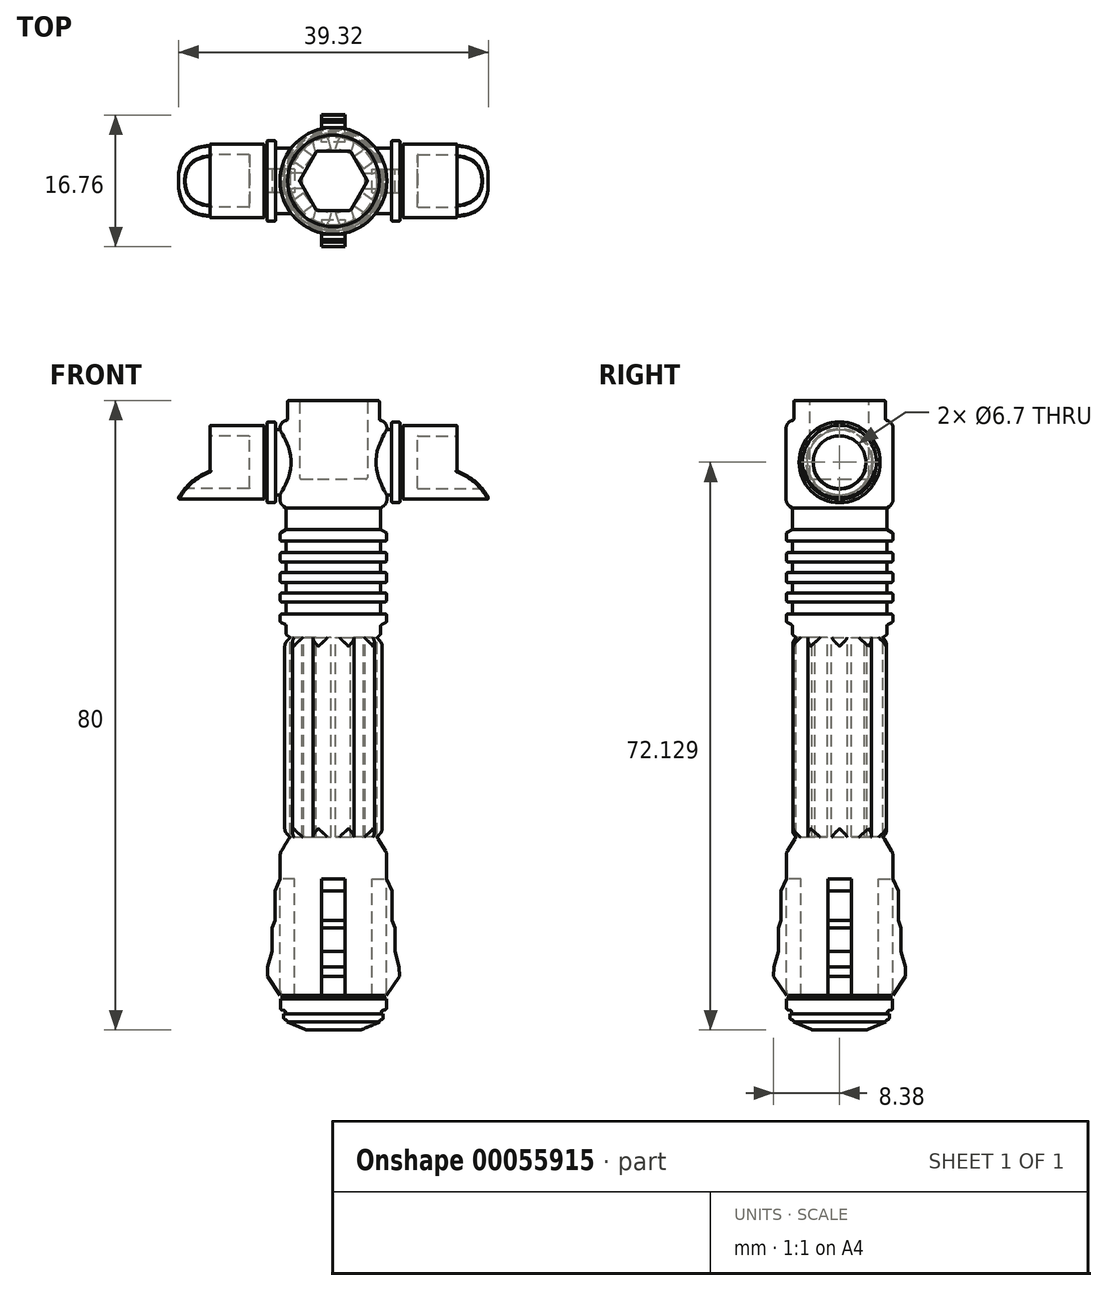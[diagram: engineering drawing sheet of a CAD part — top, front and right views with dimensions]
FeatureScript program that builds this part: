
annotation { "Feature Type Name" : "Feature", "Feature Type Description" : "" }
export const myFeature = defineFeature(function(context is Context, id is Id, definition is map)
    precondition{}
    {
        {
            var Q0;
            Q0=qCreatedBy(makeId("Front.planeOp"),FACE);
            var sketch = newSketch(context, id + "F0", { "sketchPlane" : qUnion([Q0])});
            skLineSegment(sketch, "E0", {"start": v(0, 45.09) * mm, "end": v(5.82, 45.09) * mm});
            skLineSegment(sketch, "E1", {"start": v(5.82, 45.09) * mm, "end": v(5.82, 42.56) * mm});
            skLineSegment(sketch, "E2", {"start": v(5.82, 42.56) * mm, "end": v(6.78, 42.56) * mm});
            skLineSegment(sketch, "E3", {"start": v(6.78, 42.56) * mm, "end": v(6.78, 31.92) * mm});
            skLineSegment(sketch, "E4", {"start": v(6.78, 31.92) * mm, "end": v(6, 31.43) * mm});
            skLineSegment(sketch, "E5", {"start": v(6, 31.43) * mm, "end": v(6, 28.66) * mm});
            skLineSegment(sketch, "E6", {"start": v(6, 28.66) * mm, "end": v(6.75, 28.26) * mm});
            skLineSegment(sketch, "E7", {"start": v(6.75, 28.26) * mm, "end": v(6.75, 27.2) * mm});
            skLineSegment(sketch, "E8", {"start": v(6.75, 27.2) * mm, "end": v(6, 27.2) * mm});
            skLineSegment(sketch, "E9", {"start": v(6, 27.2) * mm, "end": v(6, 25.75) * mm});
            skLineSegment(sketch, "E10", {"start": v(6, 25.75) * mm, "end": v(6.75, 25.75) * mm});
            skLineSegment(sketch, "E11", {"start": v(6.75, 25.75) * mm, "end": v(6.75, 24.56) * mm});
            skLineSegment(sketch, "E12", {"start": v(6.75, 24.56) * mm, "end": v(6, 24.56) * mm});
            skLineSegment(sketch, "E13", {"start": v(6, 24.56) * mm, "end": v(6, 23.2) * mm});
            skLineSegment(sketch, "E14", {"start": v(6, 23.2) * mm, "end": v(6.75, 23.2) * mm});
            skLineSegment(sketch, "E15", {"start": v(6.75, 23.2) * mm, "end": v(6.75, 21.94) * mm});
            skLineSegment(sketch, "E16", {"start": v(6.75, 21.94) * mm, "end": v(6, 21.94) * mm});
            skLineSegment(sketch, "E17", {"start": v(6, 21.94) * mm, "end": v(6, 20.62) * mm});
            skLineSegment(sketch, "E18", {"start": v(6, 20.62) * mm, "end": v(6.75, 20.62) * mm});
            skLineSegment(sketch, "E19", {"start": v(6.75, 20.62) * mm, "end": v(6.75, 19.49) * mm});
            skLineSegment(sketch, "E20", {"start": v(6.75, 19.49) * mm, "end": v(6, 19.49) * mm});
            skLineSegment(sketch, "E21", {"start": v(6, 19.49) * mm, "end": v(6, 17.96) * mm});
            skLineSegment(sketch, "E22", {"start": v(6, 17.96) * mm, "end": v(6.75, 17.96) * mm});
            skLineSegment(sketch, "E23", {"start": v(6.75, 17.96) * mm, "end": v(6.75, 16.93) * mm});
            skLineSegment(sketch, "E24", {"start": v(6.75, 16.93) * mm, "end": v(6, 16.54) * mm});
            skLineSegment(sketch, "E25", {"start": v(5.52, -10.4) * mm, "end": v(6.75, -12.38) * mm});
            skLineSegment(sketch, "E26", {"start": v(6.75, -12.38) * mm, "end": v(6.75, -30.53) * mm});
            skLineSegment(sketch, "E27", {"start": v(6.75, -30.53) * mm, "end": v(6.5, -30.53) * mm});
            skLineSegment(sketch, "E28", {"start": v(6.5, -30.53) * mm, "end": v(6.5, -30.96) * mm});
            skLineSegment(sketch, "E29", {"start": v(6.5, -30.96) * mm, "end": v(6.72, -30.96) * mm});
            skLineSegment(sketch, "E30", {"start": v(6.72, -30.96) * mm, "end": v(6.72, -32.3) * mm});
            skLineSegment(sketch, "E31", {"start": v(6.72, -32.3) * mm, "end": v(6.1, -32.44) * mm});
            skLineSegment(sketch, "E32", {"start": v(6.1, -32.44) * mm, "end": v(6.1, -32.85) * mm});
            skLineSegment(sketch, "E33", {"start": v(6.1, -32.85) * mm, "end": v(6.31, -32.85) * mm});
            skLineSegment(sketch, "E34", {"start": v(6.31, -32.85) * mm, "end": v(6.31, -33.5) * mm});
            skLineSegment(sketch, "E35", {"start": v(6.31, -33.5) * mm, "end": v(5.86, -33.66) * mm});
            skLineSegment(sketch, "E36", {"start": v(5.86, -33.66) * mm, "end": v(5.86, -33.9) * mm});
            skLineSegment(sketch, "E37", {"start": v(5.86, -33.9) * mm, "end": v(3.4, -34.91) * mm});
            skLineSegment(sketch, "E38", {"start": v(3.4, -34.91) * mm, "end": v(0, -34.91) * mm});
            skLineSegment(sketch, "E39", {"start": v(0, 45.09) * mm, "end": v(0, -34.91) * mm});
            skLineSegment(sketch, "E40", {"start": v(6, 16.54) * mm, "end": v(6, 15.37) * mm});
            skLineSegment(sketch, "E41", {"start": v(6, 15.37) * mm, "end": v(5.52, 14.95) * mm});
            skLineSegment(sketch, "E42", {"start": v(5.52, 14.95) * mm, "end": v(5.52, -10.4) * mm});
            skLineSegment(sketch, "E43", {"start": v(4.64, 41.35) * mm, "end": v(7.35, 41.35) * mm});
            skLineSegment(sketch, "E44", {"start": v(7.35, 41.35) * mm, "end": v(7.35, 42.36) * mm});
            skLineSegment(sketch, "E45", {"start": v(7.35, 42.36) * mm, "end": v(8.47, 42.36) * mm});
            skLineSegment(sketch, "E46", {"start": v(8.47, 42.36) * mm, "end": v(8.47, 41.5) * mm});
            skLineSegment(sketch, "E47", {"start": v(8.47, 41.5) * mm, "end": v(8.84, 41.5) * mm});
            skLineSegment(sketch, "E48", {"start": v(8.84, 41.5) * mm, "end": v(8.84, 41.91) * mm});
            skLineSegment(sketch, "E49", {"start": v(8.84, 41.91) * mm, "end": v(19.65, 41.91) * mm});
            skLineSegment(sketch, "E50", {"start": v(19.65, 41.91) * mm, "end": v(19.65, 37.22) * mm});
            skLineSegment(sketch, "E51", {"start": v(19.65, 37.22) * mm, "end": v(4.64, 37.22) * mm});
            skLineSegment(sketch, "E52", {"start": v(4.64, 37.22) * mm, "end": v(4.64, 41.35) * mm});
            skLineSegment(sketch, "E53", {"start": v(3.98, 14.95) * mm, "end": v(5.52, 14.95) * mm});
            skLineSegment(sketch, "E54", {"start": v(5.52, 14.95) * mm, "end": v(6.17, 14.21) * mm});
            skLineSegment(sketch, "E55", {"start": v(6.17, 14.21) * mm, "end": v(6.17, -9.69) * mm});
            skLineSegment(sketch, "E56", {"start": v(6.17, -9.69) * mm, "end": v(5.52, -10.4) * mm});
            skLineSegment(sketch, "E57", {"start": v(5.52, -10.4) * mm, "end": v(3.98, -10.4) * mm});
            skLineSegment(sketch, "E58", {"start": v(3.98, -10.4) * mm, "end": v(3.98, 14.95) * mm});
            skLineSegment(sketch, "E59", {"start": v(4.92, -15.72) * mm, "end": v(6.75, -15.72) * mm});
            skLineSegment(sketch, "E60", {"start": v(6.75, -15.72) * mm, "end": v(7.44, -17.24) * mm});
            skLineSegment(sketch, "E61", {"start": v(7.44, -17.24) * mm, "end": v(7.44, -20.97) * mm});
            skLineSegment(sketch, "E62", {"start": v(7.44, -20.97) * mm, "end": v(7.79, -21.93) * mm});
            skLineSegment(sketch, "E63", {"start": v(7.79, -21.93) * mm, "end": v(7.79, -24.92) * mm});
            skLineSegment(sketch, "E64", {"start": v(7.79, -24.92) * mm, "end": v(8.33, -26.9) * mm});
            skLineSegment(sketch, "E65", {"start": v(8.33, -26.9) * mm, "end": v(8.37, -28.07) * mm});
            skLineSegment(sketch, "E66", {"start": v(4.92, -30.53) * mm, "end": v(4.92, -15.72) * mm});
            skLineSegment(sketch, "E67", {"start": v(6.75, -30.53) * mm, "end": v(8.37, -28.07) * mm});
            skLineSegment(sketch, "E68", {"start": v(4.92, -30.53) * mm, "end": v(6.75, -30.53) * mm});
            skSolve(sketch);
        }
        {
            var Q0;
            Q0=makeQuery(id+"F0.imprint","IMPRINT",FACE,{"disambiguationData":[TD([[makeQuery(id+"F0.imprint","IMPRINT",EDGE,{"derivedFrom":sQuery(id+"F0.wireOp",EDGE,"E0")}),-1.0]])]});
            var Q1;
            {var subQ5=sQuery(id+"F0.wireOp",EDGE,"E52");Q1=makeQuery(id+"F0.imprint","IMPRINT",FACE,{"disambiguationData":[TD([[makeQuery(id+"F0.imprint","IMPRINT",EDGE,{"derivedFrom":subQ5}),-1.0]])]});}
            var Q2;
            Q2=makeQuery(id+"F0.imprint","IMPRINT",FACE,{"disambiguationData":[TD([[makeQuery(id+"F0.imprint","IMPRINT",EDGE,{"derivedFrom":sQuery(id+"F0.wireOp",EDGE,"E42")}),-1.0]])]});
            var Q3;
            {var subQ0=sQuery(id+"F0.wireOp",EDGE,"E59");Q3=makeQuery(id+"F0.imprint","IMPRINT",FACE,{"disambiguationData":[TD([[makeQuery(id+"F0.imprint","IMPRINT",EDGE,{"derivedFrom":subQ0}),-1.0]])]});}
            var Q4;
            Q4=sQuery(id+"F0.wireOp",EDGE,"E39");
            revolve(context, id + "F1", {"entities" : qUnion([Q0, Q1, Q2, Q3]), "axis" : qUnion([Q4]), "revolveType" : RevolveType.FULL});
        }
        {
            var Q0;
            {var subQ0=sQuery(id+"F0.wireOp",EDGE,"E44");Q0=makeQuery(id+"F0.imprint","IMPRINT",FACE,{"disambiguationData":[TD([[makeQuery(id+"F0.imprint","IMPRINT",EDGE,{"derivedFrom":subQ0}),-1.0]])]});}
            var Q1;
            {var subQ5=sQuery(id+"F0.wireOp",EDGE,"E52");Q1=makeQuery(id+"F0.imprint","IMPRINT",FACE,{"disambiguationData":[TD([[makeQuery(id+"F0.imprint","IMPRINT",EDGE,{"derivedFrom":subQ5}),-1.0]])]});}
            var Q2;
            Q2=sQuery(id+"F0.wireOp",EDGE,"E51");
            revolve(context, id + "F2", {"entities" : qUnion([Q0, Q1]), "axis" : qUnion([Q2]), "revolveType" : RevolveType.FULL});
        }
        {
            var Q0;
            Q0=makeQuery(id+"F1.opRevolve","SWEPT_FACE",FACE,{"disambiguationData":[OSD([sQuery(id+"F0.wireOp",EDGE,"E0")])]});
            var sketch = newSketch(context, id + "F3", { "sketchPlane" : qUnion([Q0])});
            skCircle(sketch, "E69.cCircle", {"center": v(0, 0) * mm, "radius": 3.75 * mm, "construction": true});
            skLineSegment(sketch, "E69.0", {"start": v(-2.17, 3.75) * mm, "end": v(2.17, 3.75) * mm});
            skLineSegment(sketch, "E69.1", {"start": v(2.17, 3.75) * mm, "end": v(4.33, 0) * mm});
            skLineSegment(sketch, "E69.2", {"start": v(4.33, 0) * mm, "end": v(2.17, -3.75) * mm});
            skLineSegment(sketch, "E69.3", {"start": v(2.17, -3.75) * mm, "end": v(-2.17, -3.75) * mm});
            skLineSegment(sketch, "E69.4", {"start": v(-2.17, -3.75) * mm, "end": v(-4.33, 0) * mm});
            skLineSegment(sketch, "E69.5", {"start": v(-4.33, 0) * mm, "end": v(-2.17, 3.75) * mm});
            skPoint(sketch, "E69.0.midPoint", {"position": v(0, 3.75) * mm});
            skSolve(sketch);
        }
        {
            var Q0;
            Q0=makeQuery(id+"F3.imprint","IMPRINT",FACE,{"disambiguationData":[TD([[makeQuery(id+"F3.imprint","IMPRINT",EDGE,{"derivedFrom":sQuery(id+"F3.wireOp",EDGE,"E69.0")}),-1.0]])]});
            extrude(context, id + "F4", {"entities" : qUnion([Q0]), "operationType" : NewBodyOperationType.REMOVE, "oppositeDirection" : true, "depth" : 10 * mm});
        }
        {
            var Q0;
            Q0=makeQuery(id+"F2.opRevolve","SWEPT_FACE",FACE,{"disambiguationData":[OSD([sQuery(id+"F0.wireOp",EDGE,"E50")])]});
            var sketch = newSketch(context, id + "F5", { "sketchPlane" : qUnion([Q0])});
            skCircle(sketch, "E70", {"center": v(0, 37.22) * mm, "radius": 3.35 * mm});
            skSolve(sketch);
        }
        {
            var Q0;
            Q0=makeQuery(id+"F5.imprint","IMPRINT",FACE,{"disambiguationData":[TD([[makeQuery(id+"F5.imprint","IMPRINT",EDGE,{"derivedFrom":sQuery(id+"F5.wireOp",EDGE,"E70")}),1.0]])]});
            extrude(context, id + "F6", {"entities" : qUnion([Q0]), "operationType" : NewBodyOperationType.REMOVE, "oppositeDirection" : true, "depth" : 9 * mm});
        }
        {
            var Q0;
            Q0=qCreatedBy(makeId("Front.planeOp"),FACE);
            var sketch = newSketch(context, id + "F7", { "sketchPlane" : qUnion([Q0])});
            skArc(sketch, "E71", {"start": v(20.04, 31.98) * mm, "mid": v(18.3, 34.5) * mm, "end": v(15.67, 36.1) * mm});
            skLineSegment(sketch, "E72", {"start": v(15.67, 36.1) * mm, "end": v(15.67, 42.8) * mm});
            skLineSegment(sketch, "E73", {"start": v(15.67, 42.8) * mm, "end": v(22.1, 42.8) * mm});
            skLineSegment(sketch, "E74", {"start": v(22.1, 42.8) * mm, "end": v(22.1, 31.92) * mm});
            skLineSegment(sketch, "E75", {"start": v(22.1, 31.92) * mm, "end": v(20.04, 31.98) * mm});
            skSolve(sketch);
        }
        {
            var Q0;
            Q0=makeQuery(id+"F7.imprint","IMPRINT",FACE,{"disambiguationData":[TD([[makeQuery(id+"F7.imprint","IMPRINT",EDGE,{"derivedFrom":sQuery(id+"F7.wireOp",EDGE,"E71")}),-1.0]])]});
            extrude(context, id + "F8", {"entities" : qUnion([Q0]), "operationType" : NewBodyOperationType.REMOVE, "endBound" : BoundingType.SYMMETRIC, "oppositeDirection" : true, "depth" : 25 * mm});
        }
        {
            var Q0;
            Q0=makeQuery(id+"F0.imprint","IMPRINT",FACE,{"disambiguationData":[TD([[makeQuery(id+"F0.imprint","IMPRINT",EDGE,{"derivedFrom":sQuery(id+"F0.wireOp",EDGE,"E42")}),1.0]])]});
            var Q1;
            Q1=makeQuery(id+"F0.imprint","IMPRINT",FACE,{"disambiguationData":[TD([[makeQuery(id+"F0.imprint","IMPRINT",EDGE,{"derivedFrom":sQuery(id+"F0.wireOp",EDGE,"E42")}),-1.0]])]});
            extrude(context, id + "F9", {"entities" : qUnion([Q0, Q1]), "endBound" : BoundingType.SYMMETRIC, "depth" : 2 * mm});
        }
        {
            var Q0;
            {var subQ0=sQuery(id+"F0.wireOp",EDGE,"E60");Q0=makeQuery(id+"F0.imprint","IMPRINT",FACE,{"disambiguationData":[TD([[makeQuery(id+"F0.imprint","IMPRINT",EDGE,{"derivedFrom":subQ0}),-1.0]])]});}
            var Q1;
            {var subQ3=sQuery(id+"F0.wireOp",EDGE,"E59");Q1=makeQuery(id+"F0.imprint","IMPRINT",FACE,{"disambiguationData":[TD([[makeQuery(id+"F0.imprint","IMPRINT",EDGE,{"derivedFrom":subQ3}),-1.0]])]});}
            extrude(context, id + "F10", {"entities" : qUnion([Q0, Q1]), "endBound" : BoundingType.SYMMETRIC, "depth" : 3 * mm});
        }
        {
            var Q0;
            Q0=makeQuery(id+"F10.opExtrude","SWEPT_FACE",FACE,{"disambiguationData":[OSD([sQuery(id+"F0.wireOp",EDGE,"E60")])]});
            var Q1;
            Q1=makeQuery(id+"F10.opExtrude","SWEPT_FACE",FACE,{"disambiguationData":[OSD([sQuery(id+"F0.wireOp",EDGE,"E61")])]});
            var Q2;
            Q2=makeQuery(id+"F10.opExtrude","SWEPT_FACE",FACE,{"disambiguationData":[OSD([sQuery(id+"F0.wireOp",EDGE,"E63")])]});
            var Q3;
            Q3=makeQuery(id+"F10.opExtrude","SWEPT_FACE",FACE,{"disambiguationData":[OSD([sQuery(id+"F0.wireOp",EDGE,"E65")])]});
            var Q4;
            Q4=makeQuery(id+"F10.opExtrude","SWEPT_FACE",FACE,{"disambiguationData":[OSD([sQuery(id+"F0.wireOp",EDGE,"E67")])]});
            var Q5;
            Q5=makeQuery(id+"F9.opExtrude","SWEPT_FACE",FACE,{"disambiguationData":[OSD([sQuery(id+"F0.wireOp",EDGE,"E55")])]});
            var Q6;
            Q6=makeQuery(id+"F1.opRevolve","SWEPT_FACE",FACE,{"disambiguationData":[OSD([sQuery(id+"F0.wireOp",EDGE,"E38")])]});
            var Q7;
            Q7=makeQuery(id+"F1.opRevolve","SWEPT_FACE",FACE,{"disambiguationData":[OSD([sQuery(id+"F0.wireOp",EDGE,"E25")])]});
            var Q8;
            Q8=makeQuery(id+"F1.opRevolve","SWEPT_FACE",FACE,{"disambiguationData":[OSD([sQuery(id+"F0.wireOp",EDGE,"E26")])]});
            var Q9;
            Q9=makeQuery(id+"F1.opRevolve","SWEPT_FACE",FACE,{"disambiguationData":[OSD([sQuery(id+"F0.wireOp",EDGE,"E3")])]});
            fillet(context, id + "F11", {"entities" : qUnion([Q0, Q1, Q2, Q3, Q4, Q5, Q6, Q7, Q8, Q9]), "radius" : 1 * mm, "tangentPropagation" : true, "allowEdgeOverflow" : false});
        }
        {
            var Q0;
            Q0=makeQuery(id+"F1.opRevolve","SWEPT_FACE",FACE,{"disambiguationData":[OSD([sQuery(id+"F0.wireOp",EDGE,"E0")])]});
            var Q1;
            Q1=makeQuery(id+"F1.opRevolve","SWEPT_FACE",FACE,{"disambiguationData":[OSD([sQuery(id+"F0.wireOp",EDGE,"E1")])]});
            var Q2;
            Q2=makeQuery(id+"F2.opRevolve","SWEPT_FACE",FACE,{"disambiguationData":[OSD([sQuery(id+"F0.wireOp",EDGE,"E43")])]});
            var Q3;
            Q3=makeQuery(id+"F4.boolean.opBoolean","COPY",FACE,{"derivedFrom":makeQuery(id+"F4.opExtrude","CAP_FACE",FACE,{"disambiguationData":[OSD([sQuery(id+"F3.wireOp",EDGE,"E69.0"),sQuery(id+"F3.wireOp",EDGE,"E69.1"),sQuery(id+"F3.wireOp",EDGE,"E69.2"),sQuery(id+"F3.wireOp",EDGE,"E69.3"),sQuery(id+"F3.wireOp",EDGE,"E69.4"),sQuery(id+"F3.wireOp",EDGE,"E69.5")])],"isStart":false})});
            var Q4;
            Q4=makeQuery(id+"F4.boolean.opBoolean","COPY",FACE,{"derivedFrom":makeQuery(id+"F4.opExtrude","SWEPT_FACE",FACE,{"disambiguationData":[OSD([sQuery(id+"F3.wireOp",EDGE,"E69.0")])]})});
            var Q5;
            Q5=makeQuery(id+"F4.boolean.opBoolean","COPY",FACE,{"derivedFrom":makeQuery(id+"F4.opExtrude","SWEPT_FACE",FACE,{"disambiguationData":[OSD([sQuery(id+"F3.wireOp",EDGE,"E69.5")])]})});
            var Q6;
            Q6=makeQuery(id+"F4.boolean.opBoolean","COPY",FACE,{"derivedFrom":makeQuery(id+"F4.opExtrude","SWEPT_FACE",FACE,{"disambiguationData":[OSD([sQuery(id+"F3.wireOp",EDGE,"E69.1")])]})});
            var Q7;
            Q7=makeQuery(id+"F4.boolean.opBoolean","COPY",FACE,{"derivedFrom":makeQuery(id+"F4.opExtrude","SWEPT_FACE",FACE,{"disambiguationData":[OSD([sQuery(id+"F3.wireOp",EDGE,"E69.2")])]})});
            var Q8;
            Q8=makeQuery(id+"F4.boolean.opBoolean","COPY",FACE,{"derivedFrom":makeQuery(id+"F4.opExtrude","SWEPT_FACE",FACE,{"disambiguationData":[OSD([sQuery(id+"F3.wireOp",EDGE,"E69.3")])]})});
            var Q9;
            Q9=makeQuery(id+"F4.boolean.opBoolean","COPY",FACE,{"derivedFrom":makeQuery(id+"F4.opExtrude","SWEPT_FACE",FACE,{"disambiguationData":[OSD([sQuery(id+"F3.wireOp",EDGE,"E69.4")])]})});
            var Q10;
            Q10=makeQuery(id+"F1.opRevolve","SWEPT_FACE",FACE,{"disambiguationData":[OSD([sQuery(id+"F0.wireOp",EDGE,"E11")])]});
            var Q11;
            Q11=makeQuery(id+"F1.opRevolve","SWEPT_FACE",FACE,{"disambiguationData":[OSD([sQuery(id+"F0.wireOp",EDGE,"E15")])]});
            var Q12;
            Q12=makeQuery(id+"F1.opRevolve","SWEPT_FACE",FACE,{"disambiguationData":[OSD([sQuery(id+"F0.wireOp",EDGE,"E19")])]});
            var Q13;
            Q13=makeQuery(id+"F1.opRevolve","SWEPT_FACE",FACE,{"disambiguationData":[OSD([sQuery(id+"F0.wireOp",EDGE,"E23")])]});
            var Q14;
            Q14=makeQuery(id+"F1.opRevolve","SWEPT_FACE",FACE,{"disambiguationData":[OSD([sQuery(id+"F0.wireOp",EDGE,"E41")])]});
            var Q15;
            Q15=makeQuery(id+"F1.opRevolve","SWEPT_FACE",FACE,{"disambiguationData":[OSD([sQuery(id+"F0.wireOp",EDGE,"E7")])]});
            var Q16;
            Q16=makeQuery(id+"F1.opRevolve","SWEPT_FACE",FACE,{"disambiguationData":[OSD([sQuery(id+"F0.wireOp",EDGE,"E9")])]});
            var Q17;
            Q17=makeQuery(id+"F1.opRevolve","SWEPT_FACE",FACE,{"disambiguationData":[OSD([sQuery(id+"F0.wireOp",EDGE,"E13")])]});
            var Q18;
            Q18=makeQuery(id+"F1.opRevolve","SWEPT_FACE",FACE,{"disambiguationData":[OSD([sQuery(id+"F0.wireOp",EDGE,"E21")])]});
            var Q19;
            Q19=makeQuery(id+"F1.opRevolve","SWEPT_FACE",FACE,{"disambiguationData":[OSD([sQuery(id+"F0.wireOp",EDGE,"E40")])]});
            var Q20;
            Q20=makeQuery(id+"F1.opRevolve","SWEPT_FACE",FACE,{"disambiguationData":[OSD([sQuery(id+"F0.wireOp",EDGE,"E31")])]});
            var Q21;
            Q21=makeQuery(id+"F1.opRevolve","SWEPT_FACE",FACE,{"disambiguationData":[OSD([sQuery(id+"F0.wireOp",EDGE,"E35")])]});
            var Q22;
            Q22=makeQuery(id+"F2.opRevolve","SWEPT_FACE",FACE,{"disambiguationData":[OSD([sQuery(id+"F0.wireOp",EDGE,"E45")])]});
            fillet(context, id + "F12", {"entities" : qUnion([Q0, Q1, Q2, Q3, Q4, Q5, Q6, Q7, Q8, Q9, Q10, Q11, Q12, Q13, Q14, Q15, Q16, Q17, Q18, Q19, Q20, Q21, Q22]), "radius" : .2 * mm, "tangentPropagation" : true, "allowEdgeOverflow" : false});
        }
        {
            var Q0;
            Q0=makeQuery(id+"F8.boolean.opBoolean","COPY",FACE,{"derivedFrom":makeQuery(id+"F8.opExtrude","SWEPT_FACE",FACE,{"disambiguationData":[OSD([sQuery(id+"F7.wireOp",EDGE,"E72")])]})});
            var Q1;
            Q1=makeQuery(id+"F2.opRevolve","SWEPT_FACE",FACE,{"disambiguationData":[OSD([sQuery(id+"F0.wireOp",EDGE,"E49")])]});
            var Q2;
            Q2=makeQuery(id+"F6.boolean.opBoolean","COPY",FACE,{"derivedFrom":makeQuery(id+"F6.opExtrude","SWEPT_FACE",FACE,{"disambiguationData":[OSD([sQuery(id+"F5.wireOp",EDGE,"E70")])]})});
            fillet(context, id + "F13", {"entities" : qUnion([Q0, Q1, Q2]), "radius" : .1 * mm, "tangentPropagation" : true, "allowEdgeOverflow" : false});
        }
        {
            var Q0;
            Q0=makeQuery(id+"F10.opExtrude","SWEPT_BODY",BODY,{"disambiguationData":[OSD([sQuery(id+"F0.wireOp",EDGE,"E59"),sQuery(id+"F0.wireOp",EDGE,"E60"),sQuery(id+"F0.wireOp",EDGE,"E61"),sQuery(id+"F0.wireOp",EDGE,"E62"),sQuery(id+"F0.wireOp",EDGE,"E63"),sQuery(id+"F0.wireOp",EDGE,"E64"),sQuery(id+"F0.wireOp",EDGE,"E65"),sQuery(id+"F0.wireOp",EDGE,"E66"),sQuery(id+"F0.wireOp",EDGE,"E67"),sQuery(id+"F0.wireOp",EDGE,"E68")])]});
            var Q1;
            {var subQ0=sQuery(id+"F0.wireOp",EDGE,"E68");var subQ1=sQuery(id+"F0.wireOp",EDGE,"E67");var subQ2=sQuery(id+"F0.wireOp",EDGE,"E26");Q1=makeQuery(id+"F11.opFillet","BLEND_FACE",FACE,{"disambiguationData":[OSD([subQ2,subQ1,subQ0]),TDD([makeQuery(id+"F1.opRevolve","SWEPT_EDGE",EDGE,{"disambiguationData":[OSD([subQ2,subQ1,subQ0])]})])]});}
            circularPattern(context, id + "F14", {"entities" : qUnion([Q0]), "axis" : qUnion([Q1]), "angle" : 90 * degree, "instanceCount" : 4});
        }
        {
            var Q0;
            Q0=makeQuery(id+"F9.opExtrude","SWEPT_BODY",BODY,{"disambiguationData":[OSD([sQuery(id+"F0.wireOp",EDGE,"E53"),sQuery(id+"F0.wireOp",EDGE,"E54"),sQuery(id+"F0.wireOp",EDGE,"E55"),sQuery(id+"F0.wireOp",EDGE,"E56"),sQuery(id+"F0.wireOp",EDGE,"E57"),sQuery(id+"F0.wireOp",EDGE,"E58")])]});
            var Q1;
            Q1=makeQuery(id+"F1.opRevolve","SWEPT_FACE",FACE,{"disambiguationData":[OSD([sQuery(id+"F0.wireOp",EDGE,"E42")])]});
            circularPattern(context, id + "F15", {"entities" : qUnion([Q0]), "axis" : qUnion([Q1]), "angle" : 36 * degree, "instanceCount" : 10});
        }
        {
            var Q0;
            Q0=makeQuery(id+"F2.opRevolve","SWEPT_BODY",BODY,{"disambiguationData":[OSD([sQuery(id+"F0.wireOp",EDGE,"E43"),sQuery(id+"F0.wireOp",EDGE,"E44"),sQuery(id+"F0.wireOp",EDGE,"E45"),sQuery(id+"F0.wireOp",EDGE,"E46"),sQuery(id+"F0.wireOp",EDGE,"E47"),sQuery(id+"F0.wireOp",EDGE,"E48"),sQuery(id+"F0.wireOp",EDGE,"E49"),sQuery(id+"F0.wireOp",EDGE,"E50"),sQuery(id+"F0.wireOp",EDGE,"E51"),sQuery(id+"F0.wireOp",EDGE,"E52")])]});
            var Q1;
            Q1=qCreatedBy(makeId("Right.planeOp"),FACE);
            mirror(context, id + "F16", {"operationType" : NewBodyOperationType.ADD, "entities" : qUnion([Q0]), "mirrorPlane" : qUnion([Q1])});
        }
    });
